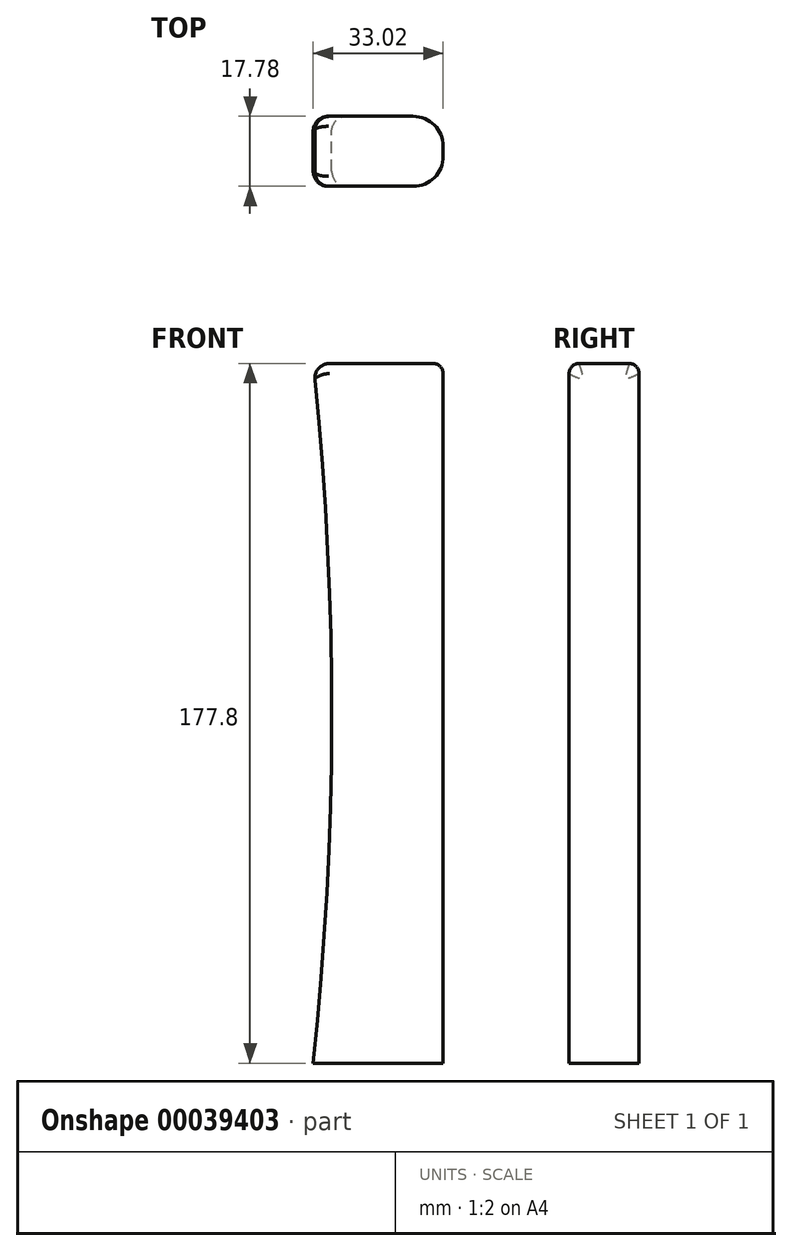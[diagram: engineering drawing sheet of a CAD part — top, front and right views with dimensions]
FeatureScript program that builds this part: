
annotation { "Feature Type Name" : "Feature", "Feature Type Description" : "" }
export const myFeature = defineFeature(function(context is Context, id is Id, definition is map)
    precondition{}
    {
        {
            var Q0;
            Q0=qCreatedBy(makeId("Front.planeOp"),FACE);
            var sketch = newSketch(context, id + "F0", { "sketchPlane" : qUnion([Q0])});
            skLineSegment(sketch, "E0", {"start": v(9.6, -144.5) * mm, "end": v(9.6, 33.3) * mm});
            skLineSegment(sketch, "E1", {"start": v(9.6, 33.3) * mm, "end": v(-23.42, 33.3) * mm});
            skLineSegment(sketch, "E2", {"start": v(9.6, -144.5) * mm, "end": v(-23.42, -144.5) * mm});
            skArc(sketch, "E3", {"start": v(-23.42, -144.5) * mm, "mid": v(-18.7, -55.6) * mm, "end": v(-23.42, 33.3) * mm});
            skSolve(sketch);
        }
        {
            var Q0;
            Q0=qSketchRegion(id+"F0",true);
            extrude(context, id + "F1", {"entities" : qUnion([Q0]), "depth" : 17.78 * mm});
        }
        {
            var Q0;
            Q0=makeQuery(id+"F1.opExtrude","CAP_EDGE",EDGE,{"disambiguationData":[OSD([sQuery(id+"F0.wireOp",EDGE,"E0")])],"isStart":false});
            var Q1;
            Q1=makeQuery(id+"F1.opExtrude","CAP_EDGE",EDGE,{"disambiguationData":[OSD([sQuery(id+"F0.wireOp",EDGE,"E0")])],"isStart":true});
            var Q2;
            Q2=makeQuery(id+"F1.opExtrude","CAP_EDGE",EDGE,{"disambiguationData":[OSD([sQuery(id+"F0.wireOp",EDGE,"367384ce-6634-46e9-a031-d25d7f5a6f8e")])],"isStart":true});
            var Q3;
            Q3=makeQuery(id+"F1.opExtrude","CAP_EDGE",EDGE,{"disambiguationData":[OSD([sQuery(id+"F0.wireOp",EDGE,"367384ce-6634-46e9-a031-d25d7f5a6f8e")])],"isStart":false});
            var Q4;
            Q4=makeQuery(id+"F1.opExtrude","CAP_EDGE",EDGE,{"disambiguationData":[OSD([sQuery(id+"F0.wireOp",EDGE,"ed93cf97-2ccb-4e51-b4c0-a1d36dc98316")])],"isStart":true});
            var Q5;
            Q5=makeQuery(id+"F1.opExtrude","CAP_EDGE",EDGE,{"disambiguationData":[OSD([sQuery(id+"F0.wireOp",EDGE,"ed93cf97-2ccb-4e51-b4c0-a1d36dc98316")])],"isStart":false});
            fillet(context, id + "F2", {"entities" : qUnion([Q0, Q1, Q2, Q3, Q4, Q5]), "radius" : 7.62 * mm, "tangentPropagation" : true, "allowEdgeOverflow" : false});
        }
        {
            var Q0;
            Q0=makeQuery(id+"F1.opExtrude","CAP_EDGE",EDGE,{"disambiguationData":[OSD([sQuery(id+"F0.wireOp",EDGE,"E1")])],"isStart":false});
            var Q1;
            Q1=makeQuery(id+"F1.opExtrude","CAP_EDGE",EDGE,{"disambiguationData":[OSD([sQuery(id+"F0.wireOp",EDGE,"E1")])],"isStart":true});
            var Q2;
            Q2=makeQuery(id+"F2.opFillet","BLEND_EDGE",EDGE,{"blendedFrom":[makeQuery(id+"F1.opExtrude","CAP_EDGE",EDGE,{"disambiguationData":[OSD([sQuery(id+"F0.wireOp",EDGE,"E0")])],"isStart":false}),makeQuery(id+"F1.opExtrude","SWEPT_FACE",FACE,{"disambiguationData":[OSD([sQuery(id+"F0.wireOp",EDGE,"E1")])]})],"blendedInto":[makeQuery(id+"F1.opExtrude","SWEPT_FACE",FACE,{"disambiguationData":[OSD([sQuery(id+"F0.wireOp",EDGE,"E1")])]})]});
            var Q3;
            Q3=makeQuery(id+"F2.opFillet","BLEND_EDGE",EDGE,{"blendedFrom":[makeQuery(id+"F1.opExtrude","CAP_EDGE",EDGE,{"disambiguationData":[OSD([sQuery(id+"F0.wireOp",EDGE,"367384ce-6634-46e9-a031-d25d7f5a6f8e")])],"isStart":false}),makeQuery(id+"F1.opExtrude","SWEPT_FACE",FACE,{"disambiguationData":[OSD([sQuery(id+"F0.wireOp",EDGE,"E1")])]})],"blendedInto":[makeQuery(id+"F1.opExtrude","SWEPT_FACE",FACE,{"disambiguationData":[OSD([sQuery(id+"F0.wireOp",EDGE,"E1")])]})]});
            var Q4;
            Q4=makeQuery(id+"F2.opFillet","BLEND_EDGE",EDGE,{"blendedFrom":[makeQuery(id+"F1.opExtrude","CAP_EDGE",EDGE,{"disambiguationData":[OSD([sQuery(id+"F0.wireOp",EDGE,"367384ce-6634-46e9-a031-d25d7f5a6f8e")])],"isStart":false}),makeQuery(id+"F1.opExtrude","SWEPT_FACE",FACE,{"disambiguationData":[OSD([sQuery(id+"F0.wireOp",EDGE,"E2")])]})],"blendedInto":[makeQuery(id+"F1.opExtrude","SWEPT_FACE",FACE,{"disambiguationData":[OSD([sQuery(id+"F0.wireOp",EDGE,"E2")])]})]});
            fillet(context, id + "F3", {"entities" : qUnion([Q0, Q1, Q2, Q3, Q4]), "radius" : 2.54 * mm, "tangentPropagation" : true, "allowEdgeOverflow" : false});
        }
        {
            var Q0;
            Q0=makeQuery(id+"F1.opExtrude","CAP_EDGE",EDGE,{"disambiguationData":[OSD([sQuery(id+"F0.wireOp",EDGE,"E3")])],"isStart":true});
            var Q1;
            Q1=makeQuery(id+"F1.opExtrude","CAP_EDGE",EDGE,{"disambiguationData":[OSD([sQuery(id+"F0.wireOp",EDGE,"E3")])],"isStart":false});
            fillet(context, id + "F4", {"entities" : qUnion([Q0, Q1]), "radius" : 3.8 * mm, "tangentPropagation" : true, "allowEdgeOverflow" : false});
        }
        {
            var Q0;
            Q0=makeQuery(id+"F1.opExtrude","SWEPT_BODY",BODY,{"disambiguationData":[OSD([sQuery(id+"F0.wireOp",EDGE,"E0"),sQuery(id+"F0.wireOp",EDGE,"E1"),sQuery(id+"F0.wireOp",EDGE,"E2"),sQuery(id+"F0.wireOp",EDGE,"E3")])]});
            transform(context, id + "F5", {"entities" : qUnion([Q0]), "transformType" : TransformType.TRANSLATION_3D, "dx" : 0 * mm, "dy" : 0 * mm, "dz" : 0 * mm, "makeCopy" : true});
        }
    });
